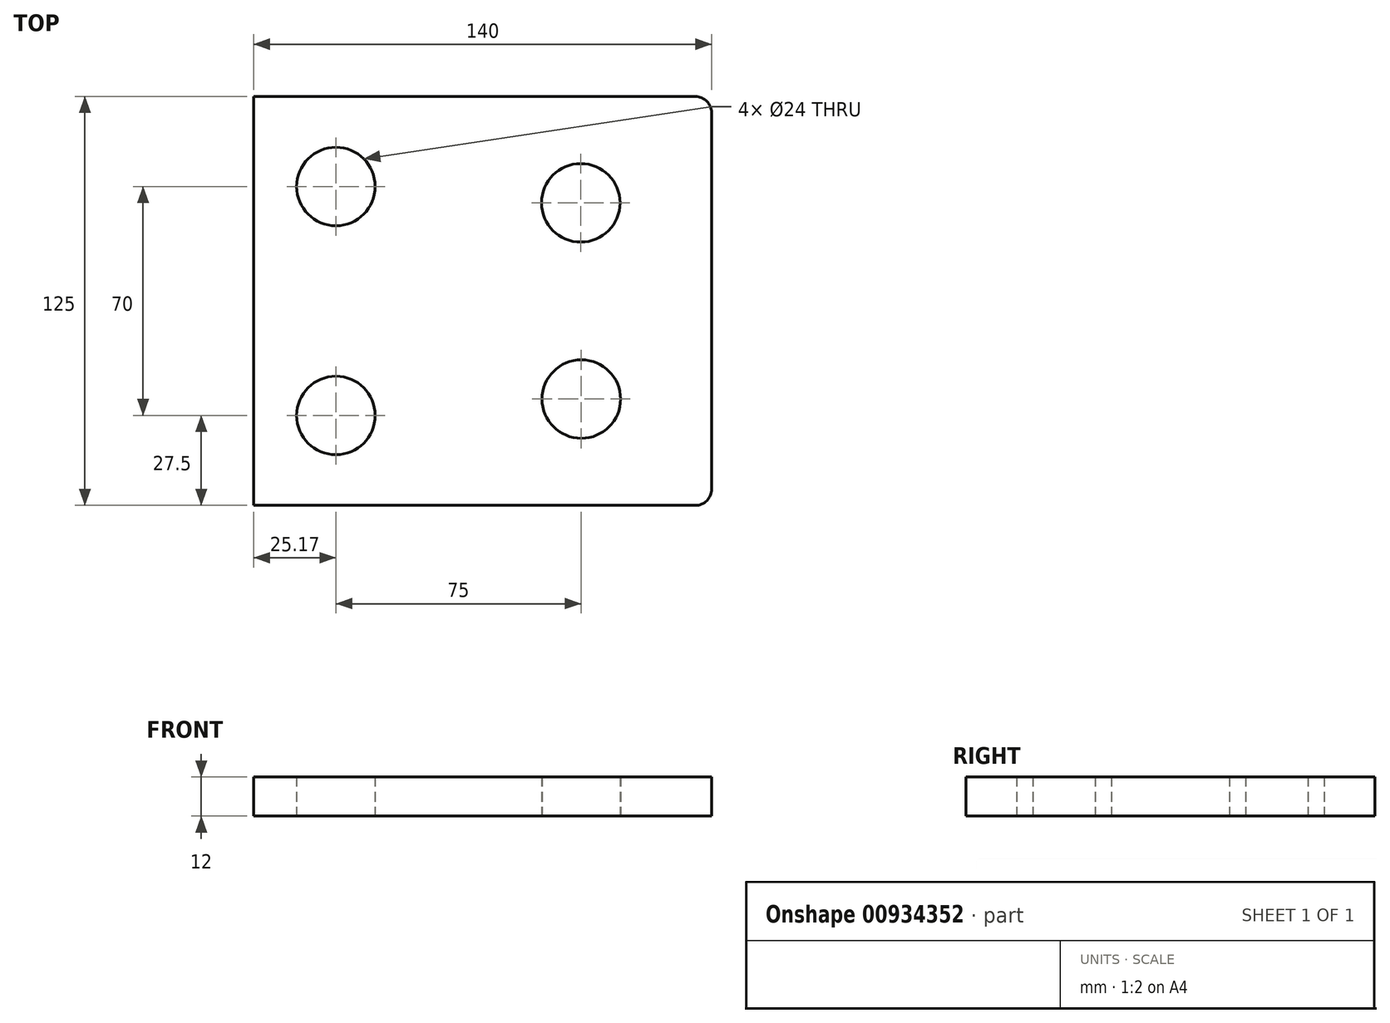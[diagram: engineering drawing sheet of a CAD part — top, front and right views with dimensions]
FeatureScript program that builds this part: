
annotation { "Feature Type Name" : "Feature", "Feature Type Description" : "" }
export const myFeature = defineFeature(function(context is Context, id is Id, definition is map)
    precondition{}
    {
        {
            var Q0;
            Q0=qCreatedBy(makeId("Top.planeOp"),FACE);
            var sketch = newSketch(context, id + "F0", { "sketchPlane" : qUnion([Q0])});
            skCircle(sketch, "E0", {"center": v(0, 35) * mm, "radius": 12 * mm});
            skCircle(sketch, "E1", {"center": v(0, -35) * mm, "radius": 12 * mm});
            skLineSegment(sketch, "E2", {"start": v(-25.17, 62.5) * mm, "end": v(109.83, 62.5) * mm});
            skLineSegment(sketch, "E3.0", {"start": v(-25.17, -62.5) * mm, "end": v(109.83, -62.5) * mm});
            skCircle(sketch, "E4", {"center": v(74.84, 30) * mm, "radius": 12 * mm});
            skCircle(sketch, "E5", {"center": v(75, -30) * mm, "radius": 12 * mm});
            skLineSegment(sketch, "E6", {"start": v(-25.17, 62.5) * mm, "end": v(-25.17, -62.5) * mm});
            skLineSegment(sketch, "E7", {"start": v(114.83, 57.5) * mm, "end": v(114.83, -57.5) * mm});
            skPoint(sketch, "E8.visualSharp", {"position": v(114.83, 62.5) * mm});
            skArc(sketch, "E8.filletArc", {"start": v(114.83, 57.5) * mm, "mid": v(113.37, 61.04) * mm, "end": v(109.83, 62.5) * mm});
            skPoint(sketch, "E9.visualSharp", {"position": v(114.83, -62.5) * mm});
            skArc(sketch, "E9.filletArc", {"start": v(109.83, -62.5) * mm, "mid": v(113.37, -61.04) * mm, "end": v(114.83, -57.5) * mm});
            skSolve(sketch);
        }
        {
            var Q0;
            Q0=makeQuery(id+"F0.imprint","IMPRINT",FACE,{"disambiguationData":[TD([[makeQuery(id+"F0.imprint","IMPRINT",EDGE,{"derivedFrom":sQuery(id+"F0.wireOp",EDGE,"E0")}),-1.0]])]});
            extrude(context, id + "F1", {"entities" : qUnion([Q0]), "depth" : 12 * mm, "offsetDistance" : 25 * mm});
        }
    });
